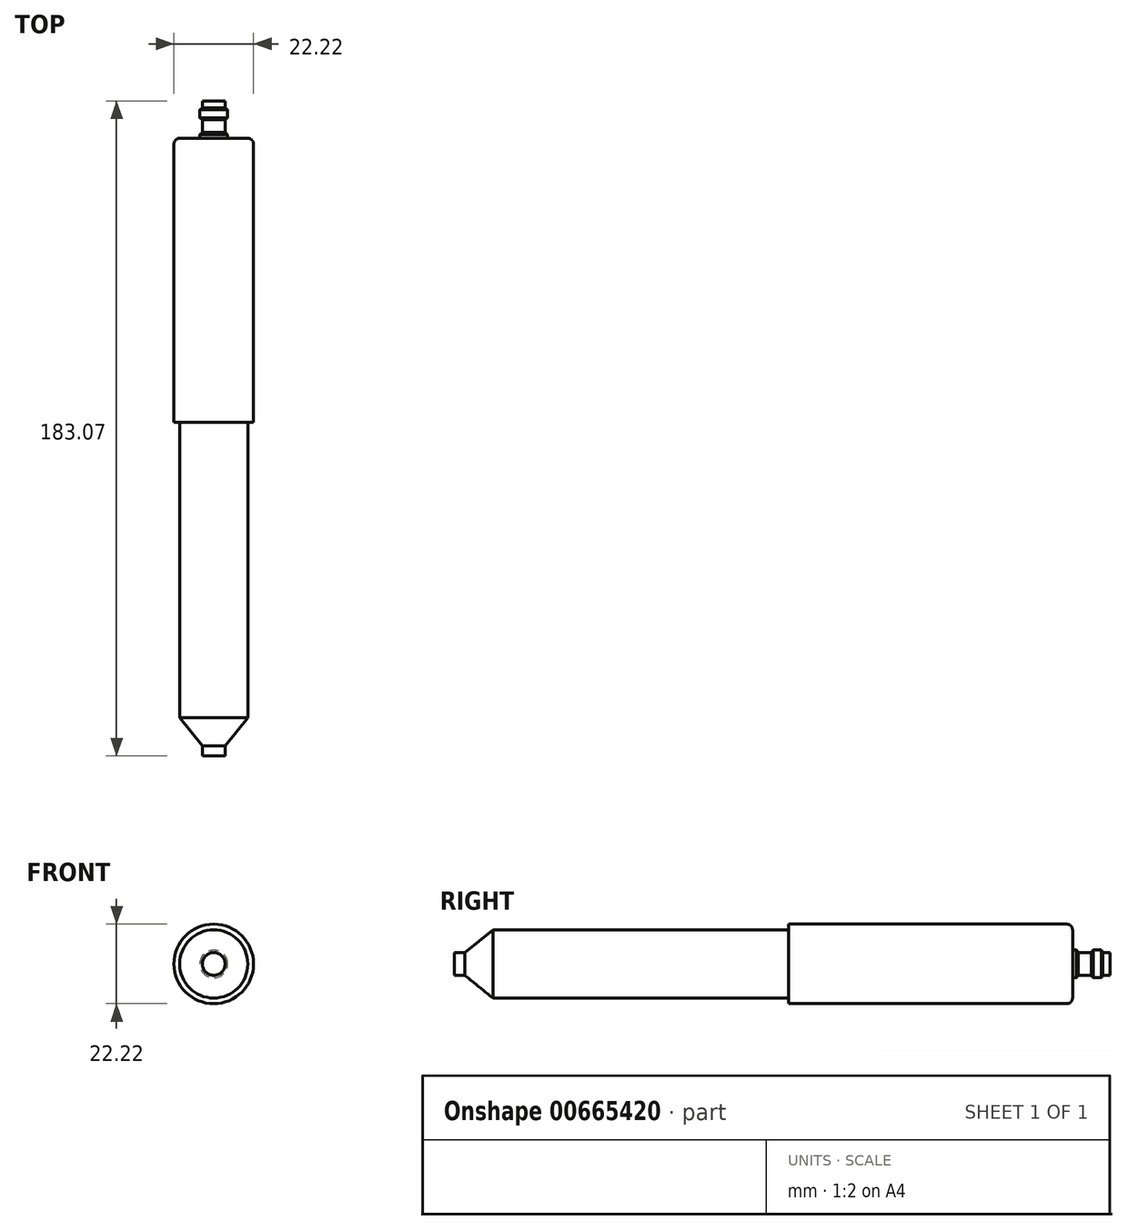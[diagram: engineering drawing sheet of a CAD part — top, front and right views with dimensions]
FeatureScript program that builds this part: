
annotation { "Feature Type Name" : "Feature", "Feature Type Description" : "" }
export const myFeature = defineFeature(function(context is Context, id is Id, definition is map)
    precondition{}
    {
        {
            var Q0;
            Q0=qCreatedBy(makeId("Right.planeOp"),FACE);
            var sketch = newSketch(context, id + "F0", { "sketchPlane" : qUnion([Q0])});
            skLineSegment(sketch, "E0", {"start": v(-56.05, 9.53) * mm, "end": v(26.5, 9.53) * mm});
            skLineSegment(sketch, "E1", {"start": v(26.5, 11.11) * mm, "end": v(105.87, 11.11) * mm});
            skLineSegment(sketch, "E2", {"start": v(105.87, 11.11) * mm, "end": v(105.87, 3.87) * mm});
            skLineSegment(sketch, "E3", {"start": v(107.51, 3.18) * mm, "end": v(111.09, 3.18) * mm});
            skLineSegment(sketch, "E4", {"start": v(116.3, 3.18) * mm, "end": v(116.3, 0) * mm});
            skLineSegment(sketch, "E5", {"start": v(114.34, 3.18) * mm, "end": v(113.93, 3.87) * mm});
            skLineSegment(sketch, "E6", {"start": v(113.93, 3.87) * mm, "end": v(111.63, 3.87) * mm});
            skLineSegment(sketch, "E7", {"start": v(111.63, 3.87) * mm, "end": v(111.09, 3.18) * mm});
            skLineSegment(sketch, "E8", {"start": v(111.09, 3.18) * mm, "end": v(107.51, 3.18) * mm});
            skLineSegment(sketch, "E9", {"start": v(107.51, 3.18) * mm, "end": v(106.94, 3.87) * mm});
            skLineSegment(sketch, "E10", {"start": v(106.94, 3.87) * mm, "end": v(105.87, 3.87) * mm});
            skLineSegment(sketch, "E11.trimOffspring", {"start": v(114.34, 3.18) * mm, "end": v(116.3, 3.18) * mm});
            skLineSegment(sketch, "E12", {"start": v(-66.77, 3.18) * mm, "end": v(-66.77, 0) * mm});
            skLineSegment(sketch, "E13", {"start": v(-66.77, 3.18) * mm, "end": v(-63.9, 3.18) * mm});
            skLineSegment(sketch, "E14", {"start": v(-63.9, 3.17) * mm, "end": v(-56.05, 9.52) * mm});
            skLineSegment(sketch, "E15", {"start": v(26.5, 9.53) * mm, "end": v(26.5, 11.11) * mm});
            skLineSegment(sketch, "E16", {"start": v(-66.77, 0) * mm, "end": v(116.3, 0) * mm});
            skSolve(sketch);
        }
        {
            var Q0;
            Q0=makeQuery(id+"F0.imprint","IMPRINT",FACE,{"disambiguationData":[TD([[makeQuery(id+"F0.imprint","IMPRINT",EDGE,{"derivedFrom":sQuery(id+"F0.wireOp",EDGE,"E0")}),-1.0]])]});
            var Q1;
            Q1=sQuery(id+"F0.wireOp",EDGE,"E16");
            revolve(context, id + "F1", {"entities" : qUnion([Q0]), "axis" : qUnion([Q1]), "revolveType" : RevolveType.FULL});
        }
        {
            var Q0;
            Q0=makeQuery(id+"F1.opRevolve","SWEPT_EDGE",EDGE,{"disambiguationData":[OSD([sQuery(id+"F0.wireOp",EDGE,"E1"),sQuery(id+"F0.wireOp",EDGE,"E2")])]});
            fillet(context, id + "F2", {"entities" : qUnion([Q0]), "radius" : 1.59 * mm, "tangentPropagation" : true, "allowEdgeOverflow" : false});
        }
    });
